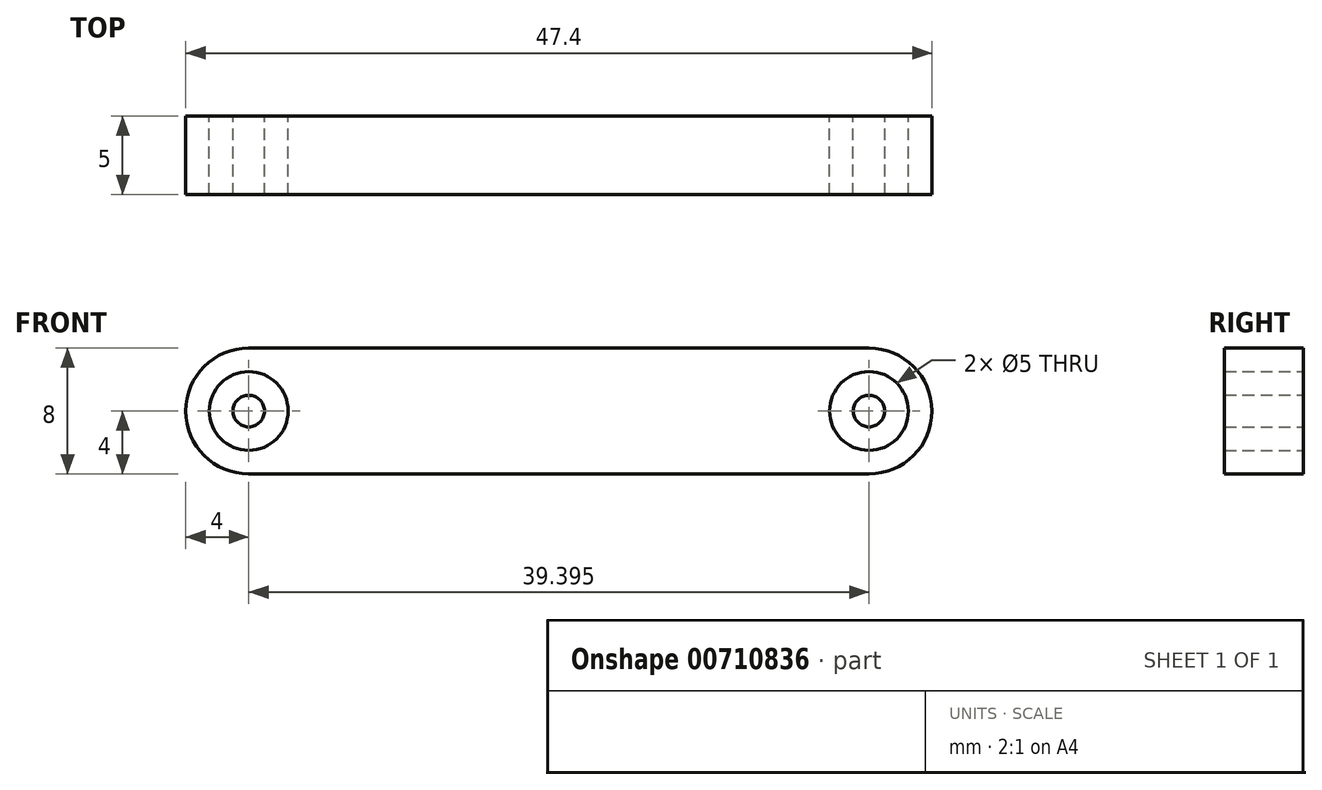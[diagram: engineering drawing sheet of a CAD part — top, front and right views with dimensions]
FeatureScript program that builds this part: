
annotation { "Feature Type Name" : "Feature", "Feature Type Description" : "" }
export const myFeature = defineFeature(function(context is Context, id is Id, definition is map)
    precondition{}
    {
        {
            var Q0;
            Q0=qCreatedBy(makeId("Front.planeOp"),FACE);
            var sketch = newSketch(context, id + "F0", { "sketchPlane" : qUnion([Q0])});
            skCircle(sketch, "E0", {"center": v(0, 0) * mm, "radius": 2.5 * mm});
            skCircle(sketch, "E1", {"center": v(0, 0) * mm, "radius": 1 * mm});
            skArc(sketch, "E2", {"start": v(0, 4) * mm, "mid": v(-4, 0) * mm, "end": v(0, -4) * mm});
            skCircle(sketch, "E3", {"center": v(39.4, 0) * mm, "radius": 1 * mm});
            skCircle(sketch, "E4", {"center": v(39.4, 0) * mm, "radius": 2.5 * mm});
            skArc(sketch, "E5", {"start": v(39.4, -4) * mm, "mid": v(43.4, 0) * mm, "end": v(39.4, 4) * mm});
            skLineSegment(sketch, "E6", {"start": v(0, 4) * mm, "end": v(39.4, 4) * mm});
            skLineSegment(sketch, "E7", {"start": v(0, -4) * mm, "end": v(39.4, -4) * mm});
            skSolve(sketch);
        }
        {
            var Q0;
            Q0=makeQuery(id+"F0.imprint","IMPRINT",FACE,{"disambiguationData":[TD([[makeQuery(id+"F0.imprint","IMPRINT",EDGE,{"derivedFrom":sQuery(id+"F0.wireOp",EDGE,"E0")}),-1.0]])]});
            var Q1;
            Q1=makeQuery(id+"F0.imprint","IMPRINT",FACE,{"disambiguationData":[TD([[makeQuery(id+"F0.imprint","IMPRINT",EDGE,{"derivedFrom":sQuery(id+"F0.wireOp",EDGE,"E1")}),1.0]])]});
            var Q2;
            Q2=makeQuery(id+"F0.imprint","IMPRINT",FACE,{"disambiguationData":[TD([[makeQuery(id+"F0.imprint","IMPRINT",EDGE,{"derivedFrom":sQuery(id+"F0.wireOp",EDGE,"E3")}),1.0]])]});
            extrude(context, id + "F1", {"entities" : qUnion([Q0, Q1, Q2]), "depth" : 5 * mm, "offsetDistance" : 25.4 * mm});
        }
    });
